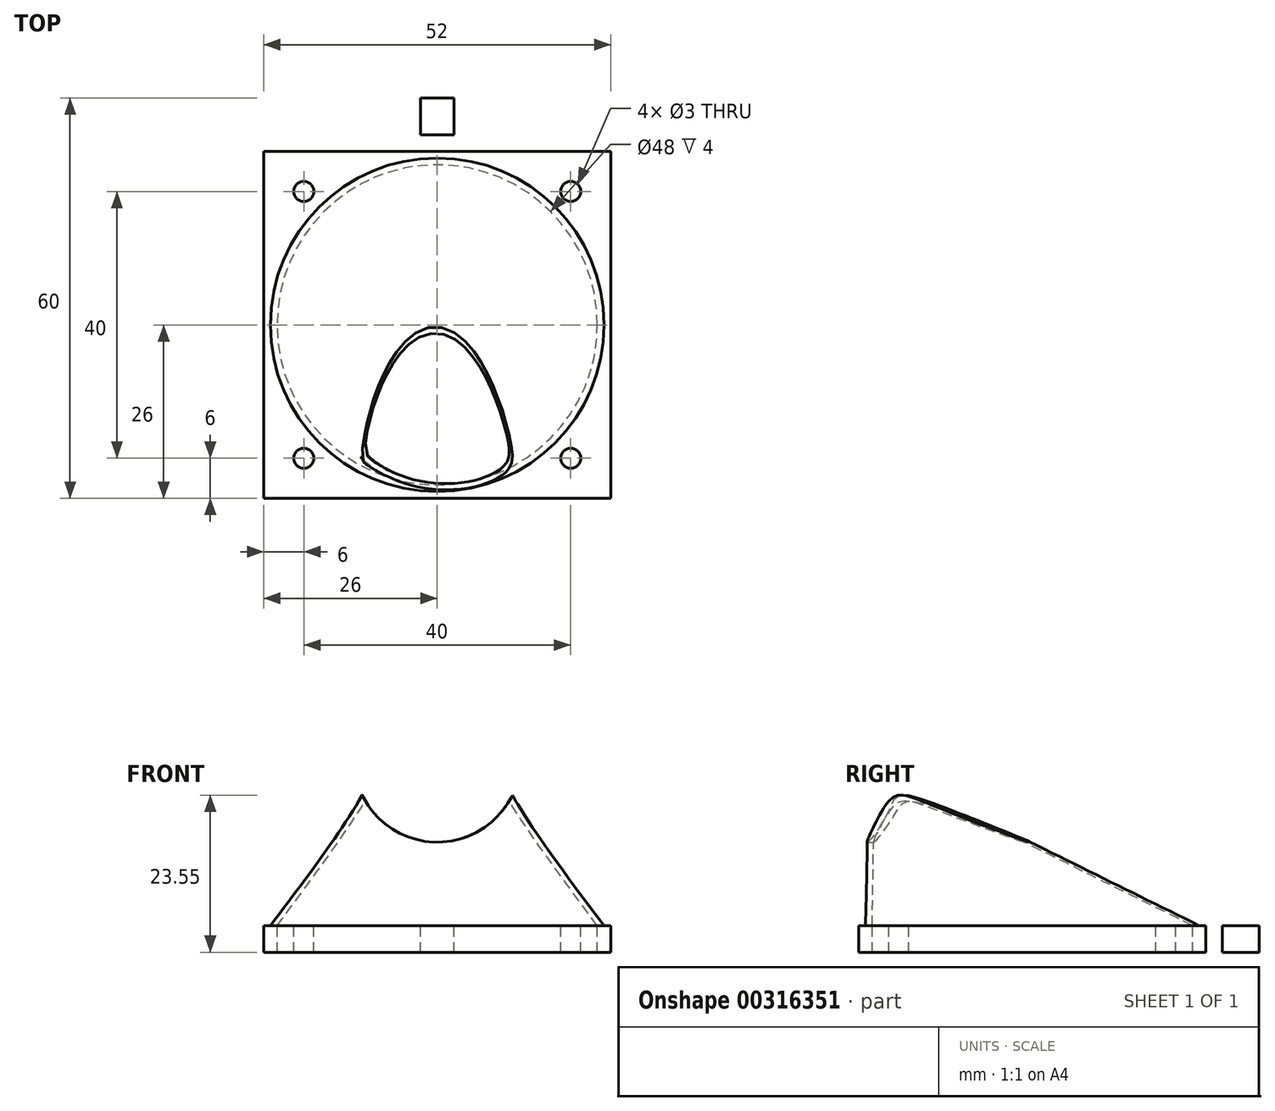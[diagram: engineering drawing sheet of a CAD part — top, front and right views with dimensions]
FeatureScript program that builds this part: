
annotation { "Feature Type Name" : "Feature", "Feature Type Description" : "" }
export const myFeature = defineFeature(function(context is Context, id is Id, definition is map)
    precondition{}
    {
        {
            var Q0;
            Q0=qCreatedBy(makeId("Top.planeOp"),FACE);
            var sketch = newSketch(context, id + "F0", { "sketchPlane" : qUnion([Q0])});
            skPoint(sketch, "E0.middle", {"position": v(0, 0) * mm});
            skCircle(sketch, "E1", {"center": v(0, 0) * mm, "radius": 24 * mm});
            skLineSegment(sketch, "E2.bottom", {"start": v(26, -26) * mm, "end": v(-26, -26) * mm});
            skLineSegment(sketch, "E2.top", {"start": v(26, 26) * mm, "end": v(-26, 26) * mm});
            skLineSegment(sketch, "E2.left", {"start": v(26, -26) * mm, "end": v(26, 26) * mm});
            skLineSegment(sketch, "E2.right", {"start": v(-26, -26) * mm, "end": v(-26, 26) * mm});
            skCircle(sketch, "E3", {"center": v(20, -20) * mm, "radius": 1.5 * mm});
            skCircle(sketch, "E4.MirrorC", {"center": v(-20, -20) * mm, "radius": 1.5 * mm});
            skCircle(sketch, "E5.MirrorC", {"center": v(20, 20) * mm, "radius": 1.5 * mm});
            skCircle(sketch, "E6.MirrorC", {"center": v(-20, 20) * mm, "radius": 1.5 * mm});
            skLineSegment(sketch, "E7.bottom", {"start": v(2.5, 26) * mm, "end": v(-2.5, 26) * mm});
            skLineSegment(sketch, "E7.top", {"start": v(2.5, 34) * mm, "end": v(-2.5, 34) * mm});
            skLineSegment(sketch, "E7.left", {"start": v(2.5, 26) * mm, "end": v(2.5, 34) * mm});
            skLineSegment(sketch, "E7.right", {"start": v(-2.5, 26) * mm, "end": v(-2.5, 34) * mm});
            skPoint(sketch, "E7.middle", {"position": v(0, 30) * mm});
            skLineSegment(sketch, "E8.0", {"start": v(2.5, 30) * mm, "end": v(-2.5, 30) * mm});
            skLineSegment(sketch, "E9.0", {"start": v(2.5, 31.5) * mm, "end": v(-2.5, 31.5) * mm});
            skLineSegment(sketch, "E10.0", {"start": v(2.5, 28.5) * mm, "end": v(-2.5, 28.5) * mm});
            skSolve(sketch);
        }
        {
            var Q0;
            Q0=qCreatedBy(makeId("Top.planeOp"),FACE);
            cPlane(context, id + "F1", {"entities" : qUnion([Q0]), "cplaneType" : CPlaneType.OFFSET, "offset" : 20 * mm, "width" : 150 * mm, "height" : 150 * mm});
        }
        {
            var Q0;
            Q0=qCreatedBy(id+"F1.planeOp",FACE);
            var sketch = newSketch(context, id + "F2", { "sketchPlane" : qUnion([Q0])});
            skEllipse(sketch, "E11", {"center": v(0, -20) * mm, "majorRadius": 10 * mm, "minorRadius": 4 * mm, "majorAxis": v(1, 0)});
            skSolve(sketch);
        }
        {
            var Q0;
            Q0=makeQuery(id+"F0.imprint","IMPRINT",FACE,{"disambiguationData":[TD([[makeQuery(id+"F0.imprint","IMPRINT",EDGE,{"derivedFrom":sQuery(id+"F0.wireOp",EDGE,"E1")}),1.0]])]});
            var Q1;
            Q1=makeQuery(id+"F2.imprint","IMPRINT",FACE,{"disambiguationData":[TD([[makeQuery(id+"F2.imprint","IMPRINT",EDGE,{"derivedFrom":sQuery(id+"F2.wireOp",EDGE,"E11")}),1.0]])]});
            loft(context, id + "F3", {"sheetProfilesArray" : [{ "sheetProfileEntities" : qUnion([Q0]) }, { "sheetProfileEntities" : qUnion([Q1]) }]});
        }
        {
            var Q0;
            Q0=qCreatedBy(makeId("Top.planeOp"),FACE);
            var sketch = newSketch(context, id + "F4", { "sketchPlane" : qUnion([Q0])});
            skCircle(sketch, "E12", {"center": v(0, 0) * mm, "radius": 25 * mm});
            skSolve(sketch);
        }
        {
            var Q0;
            Q0=qCreatedBy(id+"F1.planeOp",FACE);
            var sketch = newSketch(context, id + "F5", { "sketchPlane" : qUnion([Q0])});
            skEllipse(sketch, "E13", {"center": v(0, -20) * mm, "majorRadius": 11 * mm, "minorRadius": 5 * mm, "majorAxis": v(1, 0)});
            skSolve(sketch);
        }
        {
            var Q1;
            Q1=makeQuery(id+"F4.imprint","IMPRINT",FACE,{"disambiguationData":[TD([[makeQuery(id+"F4.imprint","IMPRINT",EDGE,{"derivedFrom":sQuery(id+"F4.wireOp",EDGE,"E12")}),1.0]])]});
            var Q2;
            Q2=makeQuery(id+"F5.imprint","IMPRINT",FACE,{"disambiguationData":[TD([[makeQuery(id+"F5.imprint","IMPRINT",EDGE,{"derivedFrom":sQuery(id+"F5.wireOp",EDGE,"E13")}),1.0]])]});
            loft(context, id + "F6", {"sheetProfilesArray" : [{ "sheetProfileEntities" : qUnion([Q1]) }, { "sheetProfileEntities" : qUnion([Q2]) }]});
        }
        {
            var Q0;
            Q0=makeQuery(id+"F3.opLoft","SWEPT_BODY",BODY,{"disambiguationData":[OSD([makeQuery(id+"F0.imprint","IMPRINT",FACE,{"disambiguationData":[TD([[makeQuery(id+"F0.imprint","IMPRINT",EDGE,{"derivedFrom":sQuery(id+"F0.wireOp",EDGE,"E1")}),1.0]])]}),makeQuery(id+"F2.imprint","IMPRINT",FACE,{"disambiguationData":[TD([[makeQuery(id+"F2.imprint","IMPRINT",EDGE,{"derivedFrom":sQuery(id+"F2.wireOp",EDGE,"E11")}),1.0]])]})])]});
            var Q1;
            Q1=makeQuery(id+"F6.opLoft","SWEPT_BODY",BODY,{"disambiguationData":[OSD([makeQuery(id+"F4.imprint","IMPRINT",FACE,{"disambiguationData":[TD([[makeQuery(id+"F4.imprint","IMPRINT",EDGE,{"derivedFrom":sQuery(id+"F4.wireOp",EDGE,"E12")}),1.0]])]}),makeQuery(id+"F5.imprint","IMPRINT",FACE,{"disambiguationData":[TD([[makeQuery(id+"F5.imprint","IMPRINT",EDGE,{"derivedFrom":sQuery(id+"F5.wireOp",EDGE,"E13")}),1.0]])]})])]});
            booleanBodies(context, id + "F7", {"operationType" : BooleanOperationType.SUBTRACTION, "tools" : qUnion([Q0]), "targets" : qUnion([Q1])});
        }
        {
            var Q0;
            Q0=makeQuery(id+"F0.imprint","IMPRINT",FACE,{"disambiguationData":[TD([[makeQuery(id+"F0.imprint","IMPRINT",EDGE,{"derivedFrom":sQuery(id+"F0.wireOp",EDGE,"E1")}),-1.0]])]});
            var Q1;
            {var subQ0=sQuery(id+"F0.wireOp",EDGE,"E7.bottom");Q1=makeQuery(id+"F0.imprint","IMPRINT",FACE,{"disambiguationData":[TD([[makeQuery(id+"F0.imprint","IMPRINT",EDGE,{"derivedFrom":subQ0}),-1.0]])]});}
            var Q2;
            {var subQ0=sQuery(id+"F0.wireOp",EDGE,"E8.0");Q2=makeQuery(id+"F0.imprint","IMPRINT",FACE,{"disambiguationData":[TD([[makeQuery(id+"F0.imprint","IMPRINT",EDGE,{"derivedFrom":subQ0}),1.0]])]});}
            var Q3;
            {var subQ0=sQuery(id+"F0.wireOp",EDGE,"E8.0");Q3=makeQuery(id+"F0.imprint","IMPRINT",FACE,{"disambiguationData":[TD([[makeQuery(id+"F0.imprint","IMPRINT",EDGE,{"derivedFrom":subQ0}),-1.0]])]});}
            var Q4;
            {var subQ0=sQuery(id+"F0.wireOp",EDGE,"E7.top");Q4=makeQuery(id+"F0.imprint","IMPRINT",FACE,{"disambiguationData":[TD([[makeQuery(id+"F0.imprint","IMPRINT",EDGE,{"derivedFrom":subQ0}),1.0]])]});}
            extrude(context, id + "F8", {"entities" : qUnion([Q0, Q1, Q2, Q3, Q4]), "operationType" : NewBodyOperationType.ADD, "oppositeDirection" : true, "depth" : 4 * mm});
        }
        {
            var Q0;
            {var subQ0=sQuery(id+"F0.wireOp",EDGE,"E8.0");Q0=makeQuery(id+"F0.imprint","IMPRINT",FACE,{"disambiguationData":[TD([[makeQuery(id+"F0.imprint","IMPRINT",EDGE,{"derivedFrom":subQ0}),1.0]])]});}
            var Q1;
            Q1=sQuery(id+"F0.wireOp",EDGE,"E8.0");
            revolve(context, id + "F9", {"entities" : qUnion([Q0]), "axis" : qUnion([Q1]), "revolveType" : RevolveType.FULL});
        }
        {
            var Q0;
            Q0=makeQuery(id+"F9.opRevolve","SWEPT_BODY",BODY,{"disambiguationData":[OSD([sQuery(id+"F0.wireOp",EDGE,"E7.left"),sQuery(id+"F0.wireOp",EDGE,"E7.right"),sQuery(id+"F0.wireOp",EDGE,"E8.0"),sQuery(id+"F0.wireOp",EDGE,"E10.0")])]});
            transform(context, id + "F10", {"entities" : qUnion([Q0]), "transformType" : TransformType.TRANSLATION_3D, "dx" : 0 * mm, "dy" : 0 * mm, "dz" : -2 * mm, "makeCopy" : false});
        }
        {
            var Q0;
            Q0=makeQuery(id+"F9.opRevolve","SWEPT_BODY",BODY,{"disambiguationData":[OSD([sQuery(id+"F0.wireOp",EDGE,"E7.left"),sQuery(id+"F0.wireOp",EDGE,"E7.right"),sQuery(id+"F0.wireOp",EDGE,"E8.0"),sQuery(id+"F0.wireOp",EDGE,"E10.0")])]});
            var Q1;
            Q1=makeQuery(id+"F6.opLoft","SWEPT_BODY",BODY,{"disambiguationData":[OSD([makeQuery(id+"F4.imprint","IMPRINT",FACE,{"disambiguationData":[TD([[makeQuery(id+"F4.imprint","IMPRINT",EDGE,{"derivedFrom":sQuery(id+"F4.wireOp",EDGE,"E12")}),1.0]])]}),makeQuery(id+"F5.imprint","IMPRINT",FACE,{"disambiguationData":[TD([[makeQuery(id+"F5.imprint","IMPRINT",EDGE,{"derivedFrom":sQuery(id+"F5.wireOp",EDGE,"E13")}),1.0]])]})])]});
            booleanBodies(context, id + "F11", {"operationType" : BooleanOperationType.SUBTRACTION, "tools" : qUnion([Q0]), "targets" : qUnion([Q1])});
        }
        {
            var Q0;
            Q0=qCreatedBy(makeId("Front.planeOp"),FACE);
            var sketch = newSketch(context, id + "F12", { "sketchPlane" : qUnion([Q0])});
            skCircle(sketch, "E14", {"center": v(0, 25) * mm, "radius": 12.5 * mm});
            skSolve(sketch);
        }
        {
            var Q0;
            Q0=makeQuery(id+"F12.imprint","IMPRINT",FACE,{"disambiguationData":[TD([[makeQuery(id+"F12.imprint","IMPRINT",EDGE,{"derivedFrom":sQuery(id+"F12.wireOp",EDGE,"E14")}),1.0]])]});
            extrude(context, id + "F13", {"entities" : qUnion([Q0]), "operationType" : NewBodyOperationType.REMOVE, "depth" : 30 * mm});
        }
    });
